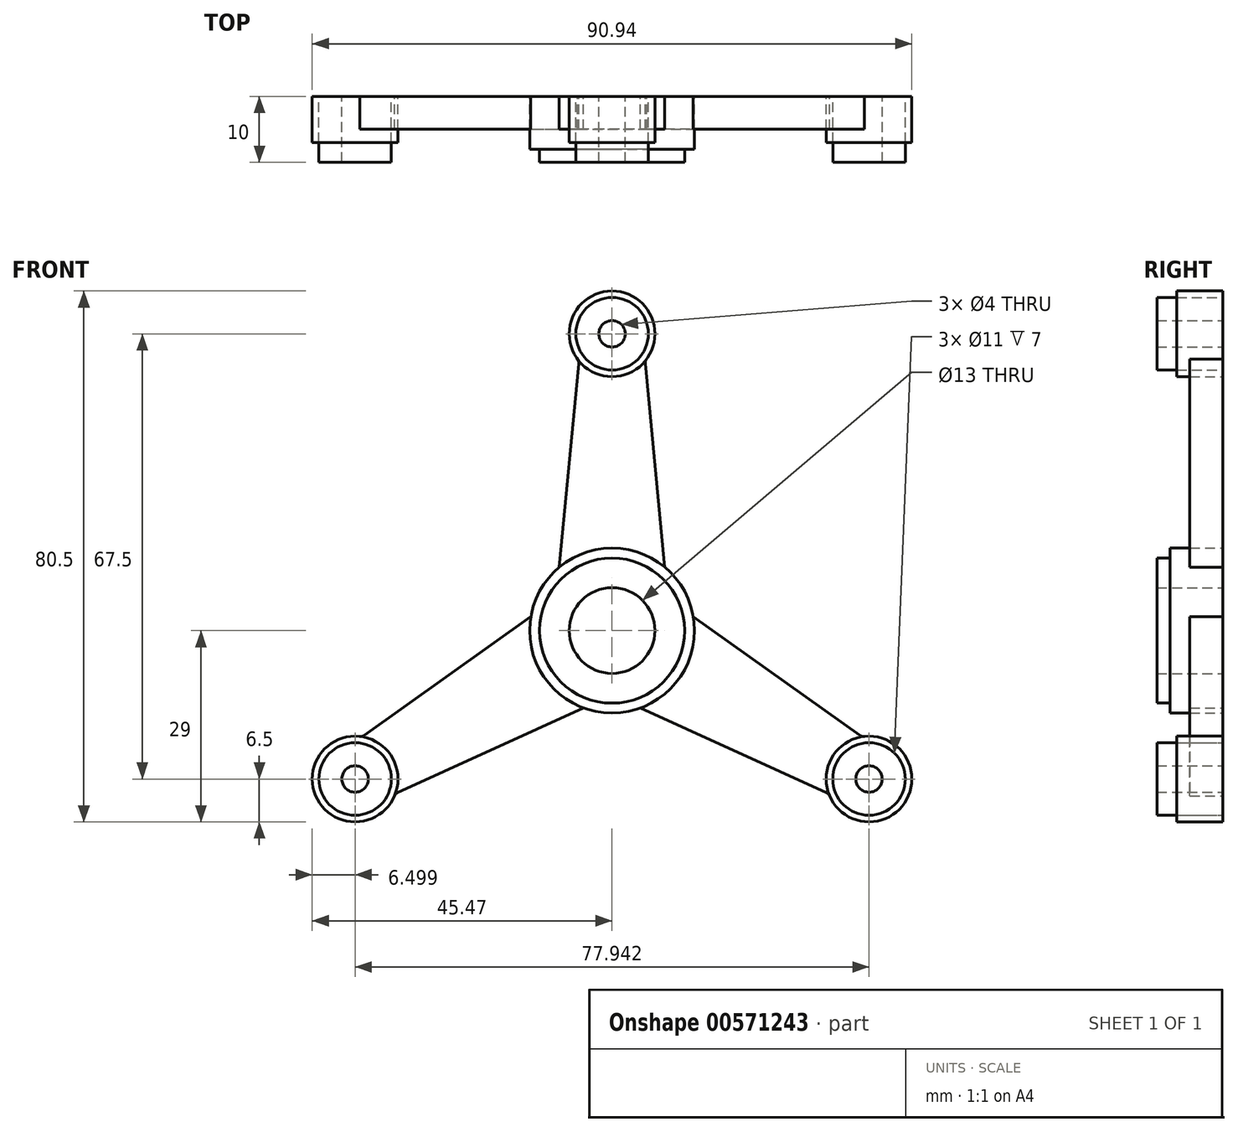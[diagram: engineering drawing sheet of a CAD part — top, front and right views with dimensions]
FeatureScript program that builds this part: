
annotation { "Feature Type Name" : "Feature", "Feature Type Description" : "" }
export const myFeature = defineFeature(function(context is Context, id is Id, definition is map)
    precondition{}
    {
        {
            var Q0;
            Q0=qCreatedBy(makeId("Front.planeOp"),FACE);
            var sketch = newSketch(context, id + "F0", { "sketchPlane" : qUnion([Q0])});
            skCircle(sketch, "E0", {"center": v(0, 0) * mm, "radius": 6.5 * mm});
            skCircle(sketch, "E1", {"center": v(0, 0) * mm, "radius": 11 * mm});
            skCircle(sketch, "E2", {"center": v(0, 0) * mm, "radius": 12.5 * mm});
            skCircle(sketch, "E3", {"center": v(0, 45) * mm, "radius": 2 * mm});
            skCircle(sketch, "E4", {"center": v(0, 45) * mm, "radius": 5.5 * mm});
            skCircle(sketch, "E5", {"center": v(0, 45) * mm, "radius": 6.5 * mm});
            skLineSegment(sketch, "E6", {"start": v(5.04, 40.45) * mm, "end": v(8, 9.6) * mm});
            skLineSegment(sketch, "E7", {"start": v(-5.04, 40.45) * mm, "end": v(-8, 9.6) * mm});
            skArc(sketch, "E8", {"start": v(5.23, 41.14) * mm, "mid": v(5.07, 40.81) * mm, "end": v(5.04, 40.45) * mm});
            skPoint(sketch, "E8.first.point", {"position": v(5.23, 41.14) * mm});
            skPoint(sketch, "E8.second.point", {"position": v(5.04, 40.45) * mm});
            skPoint(sketch, "E8.third.point", {"position": v(5.92, 39.55) * mm});
            skPoint(sketch, "E9.orphan", {"position": v(5, 40.85) * mm});
            skArc(sketch, "E10", {"start": v(-5.04, 40.45) * mm, "mid": v(-5.07, 40.81) * mm, "end": v(-5.23, 41.14) * mm});
            skPoint(sketch, "E10.first.point", {"position": v(-5.23, 41.14) * mm});
            skPoint(sketch, "E10.second.point", {"position": v(-5.04, 40.45) * mm});
            skPoint(sketch, "E10.third.point", {"position": v(-6.93, 40.1) * mm});
            skPoint(sketch, "E11.orphan", {"position": v(-5, 40.85) * mm});
            skCircle(sketch, "E12", {"center": v(0, 0) * mm, "radius": 45 * mm, "construction": true});
            skLineSegment(sketch, "E13.1.0", {"start": v(-32.51, -24.59) * mm, "end": v(-4.32, -11.73) * mm});
            skPoint(sketch, "E13.1.1", {"position": v(-32.51, -24.59) * mm});
            skPoint(sketch, "E13.1.2", {"position": v(-31.26, -26.05) * mm});
            skPoint(sketch, "E13.1.3", {"position": v(-33.01, -25.1) * mm});
            skPoint(sketch, "E13.1.4", {"position": v(-37.55, -15.86) * mm});
            skPoint(sketch, "E13.1.5", {"position": v(-37.21, -14.65) * mm});
            skLineSegment(sketch, "E13.1.6", {"start": v(-37.55, -15.86) * mm, "end": v(-12.32, 2.13) * mm});
            skPoint(sketch, "E13.1.7", {"position": v(-38.24, -16.04) * mm});
            skCircle(sketch, "E13.1.8", {"center": v(-38.97, -22.5) * mm, "radius": 6.5 * mm});
            skCircle(sketch, "E13.1.9", {"center": v(-38.97, -22.5) * mm, "radius": 5.5 * mm});
            skCircle(sketch, "E13.1.10", {"center": v(-38.97, -22.5) * mm, "radius": 2 * mm});
            skPoint(sketch, "E13.1.11", {"position": v(-32.87, -24.75) * mm});
            skPoint(sketch, "E13.1.12", {"position": v(-37.87, -16.1) * mm});
            skArc(sketch, "E13.1.13", {"start": v(-38.24, -16.04) * mm, "mid": v(-37.88, -16.02) * mm, "end": v(-37.55, -15.86) * mm});
            skArc(sketch, "E13.1.14", {"start": v(-32.51, -24.59) * mm, "mid": v(-32.8, -24.8) * mm, "end": v(-33.01, -25.1) * mm});
            skLineSegment(sketch, "E13.2.0", {"start": v(37.55, -15.86) * mm, "end": v(12.32, 2.13) * mm});
            skPoint(sketch, "E13.2.1", {"position": v(37.55, -15.86) * mm});
            skPoint(sketch, "E13.2.2", {"position": v(38.2, -14.05) * mm});
            skPoint(sketch, "E13.2.3", {"position": v(38.24, -16.04) * mm});
            skPoint(sketch, "E13.2.4", {"position": v(32.51, -24.59) * mm});
            skPoint(sketch, "E13.2.5", {"position": v(31.3, -24.9) * mm});
            skLineSegment(sketch, "E13.2.6", {"start": v(32.51, -24.59) * mm, "end": v(4.32, -11.73) * mm});
            skPoint(sketch, "E13.2.7", {"position": v(33.01, -25.1) * mm});
            skCircle(sketch, "E13.2.8", {"center": v(38.97, -22.5) * mm, "radius": 6.5 * mm});
            skCircle(sketch, "E13.2.9", {"center": v(38.97, -22.5) * mm, "radius": 5.5 * mm});
            skCircle(sketch, "E13.2.10", {"center": v(38.97, -22.5) * mm, "radius": 2 * mm});
            skPoint(sketch, "E13.2.11", {"position": v(37.87, -16.1) * mm});
            skPoint(sketch, "E13.2.12", {"position": v(32.87, -24.75) * mm});
            skArc(sketch, "E13.2.13", {"start": v(33.01, -25.1) * mm, "mid": v(32.8, -24.8) * mm, "end": v(32.51, -24.59) * mm});
            skArc(sketch, "E13.2.14", {"start": v(37.55, -15.86) * mm, "mid": v(37.88, -16.02) * mm, "end": v(38.24, -16.04) * mm});
            skSolve(sketch);
        }
        {
            var Q0;
            {var subQ0=sQuery(id+"F0.wireOp",EDGE,"E6");Q0=makeQuery(id+"F0.imprint","IMPRINT",FACE,{"disambiguationData":[TD([[makeQuery(id+"F0.imprint","IMPRINT",EDGE,{"derivedFrom":subQ0}),-1.0]])]});}
            var Q1;
            {var subQ4=sQuery(id+"F0.wireOp",EDGE,"E13.2.0");Q1=makeQuery(id+"F0.imprint","IMPRINT",FACE,{"disambiguationData":[TD([[makeQuery(id+"F0.imprint","IMPRINT",EDGE,{"derivedFrom":subQ4}),1.0]])]});}
            var Q2;
            {var subQ4=sQuery(id+"F0.wireOp",EDGE,"E13.1.0");Q2=makeQuery(id+"F0.imprint","IMPRINT",FACE,{"disambiguationData":[TD([[makeQuery(id+"F0.imprint","IMPRINT",EDGE,{"derivedFrom":subQ4}),1.0]])]});}
            extrude(context, id + "F1", {"entities" : qUnion([Q0, Q1, Q2]), "depth" : 5 * mm, "offsetDistance" : 25 * mm});
        }
        {
            var Q0;
            Q0=makeQuery(id+"F0.imprint","IMPRINT",FACE,{"disambiguationData":[TD([[makeQuery(id+"F0.imprint","IMPRINT",EDGE,{"derivedFrom":sQuery(id+"F0.wireOp",EDGE,"E1")}),-1.0]])]});
            extrude(context, id + "F2", {"entities" : qUnion([Q0]), "depth" : 8 * mm, "offsetDistance" : 25 * mm});
        }
        {
            var Q0;
            Q0=makeQuery(id+"F0.imprint","IMPRINT",FACE,{"disambiguationData":[TD([[makeQuery(id+"F0.imprint","IMPRINT",EDGE,{"derivedFrom":sQuery(id+"F0.wireOp",EDGE,"E0")}),-1.0]])]});
            extrude(context, id + "F3", {"entities" : qUnion([Q0]), "operationType" : NewBodyOperationType.ADD, "depth" : 10 * mm, "offsetDistance" : 25 * mm});
        }
        {
            var Q0;
            Q0=makeQuery(id+"F0.imprint","IMPRINT",FACE,{"disambiguationData":[TD([[makeQuery(id+"F0.imprint","IMPRINT",EDGE,{"derivedFrom":sQuery(id+"F0.wireOp",EDGE,"E13.1.9")}),-1.0]])]});
            var Q1;
            Q1=makeQuery(id+"F0.imprint","IMPRINT",FACE,{"disambiguationData":[TD([[makeQuery(id+"F0.imprint","IMPRINT",EDGE,{"derivedFrom":sQuery(id+"F0.wireOp",EDGE,"E13.2.9")}),-1.0]])]});
            var Q2;
            Q2=makeQuery(id+"F0.imprint","IMPRINT",FACE,{"disambiguationData":[TD([[makeQuery(id+"F0.imprint","IMPRINT",EDGE,{"derivedFrom":sQuery(id+"F0.wireOp",EDGE,"E4")}),-1.0]])]});
            extrude(context, id + "F4", {"entities" : qUnion([Q0, Q1, Q2]), "depth" : 7 * mm, "offsetDistance" : 25 * mm});
        }
        {
            var Q0;
            Q0=makeQuery(id+"F0.imprint","IMPRINT",FACE,{"disambiguationData":[TD([[makeQuery(id+"F0.imprint","IMPRINT",EDGE,{"derivedFrom":sQuery(id+"F0.wireOp",EDGE,"E3")}),-1.0]])]});
            var Q1;
            Q1=makeQuery(id+"F0.imprint","IMPRINT",FACE,{"disambiguationData":[TD([[makeQuery(id+"F0.imprint","IMPRINT",EDGE,{"derivedFrom":sQuery(id+"F0.wireOp",EDGE,"E13.2.9")}),1.0]])]});
            var Q2;
            Q2=makeQuery(id+"F0.imprint","IMPRINT",FACE,{"disambiguationData":[TD([[makeQuery(id+"F0.imprint","IMPRINT",EDGE,{"derivedFrom":sQuery(id+"F0.wireOp",EDGE,"E13.1.9")}),1.0]])]});
            extrude(context, id + "F5", {"entities" : qUnion([Q0, Q1, Q2]), "depth" : 10 * mm, "offsetDistance" : 25 * mm});
        }
    });
